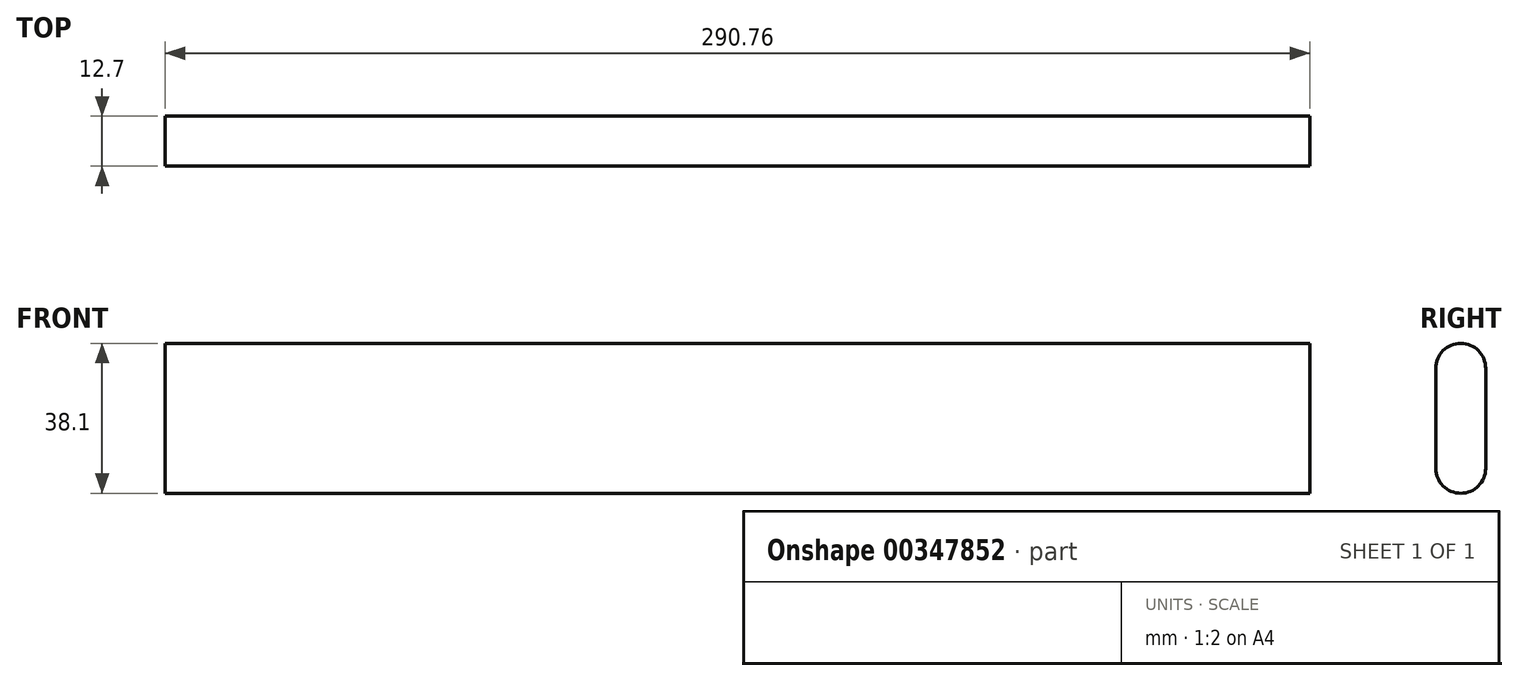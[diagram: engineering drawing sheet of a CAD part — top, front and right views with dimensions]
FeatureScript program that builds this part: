
annotation { "Feature Type Name" : "Feature", "Feature Type Description" : "" }
export const myFeature = defineFeature(function(context is Context, id is Id, definition is map)
    precondition{}
    {
        {
            var Q0;
            Q0=qCreatedBy(makeId("Right.planeOp"),FACE);
            var sketch = newSketch(context, id + "F0", { "sketchPlane" : qUnion([Q0])});
            skLineSegment(sketch, "E0.left", {"start": v(-6.35, 12.8) * mm, "end": v(-6.35, -12.6) * mm});
            skLineSegment(sketch, "E0.right", {"start": v(6.35, 12.8) * mm, "end": v(6.35, -12.6) * mm});
            skPoint(sketch, "E0.middle", {"position": v(0, 0.1) * mm});
            skLineSegment(sketch, "E1", {"start": v(0, 0.1) * mm, "end": v(0, 18.12) * mm, "construction": true});
            skPoint(sketch, "E1.endSnap0", {"position": v(0, 12.8) * mm});
            skLineSegment(sketch, "E2", {"start": v(0, 0) * mm, "end": v(0, -18) * mm, "construction": true});
            skArc(sketch, "E3", {"start": v(6.35, 12.8) * mm, "mid": v(0, 19.15) * mm, "end": v(-6.35, 12.8) * mm});
            skArc(sketch, "E4", {"start": v(-6.35, -12.6) * mm, "mid": v(0, -18.95) * mm, "end": v(6.35, -12.6) * mm});
            skSolve(sketch);
        }
        {
            var Q0;
            Q0 = qSketchRegion(id + "F0", true);
            extrude(context, id + "F1", {"entities" : qUnion([Q0]), "endBound" : BoundingType.SYMMETRIC, "depth" : 290.76 * mm});
        }
    });
